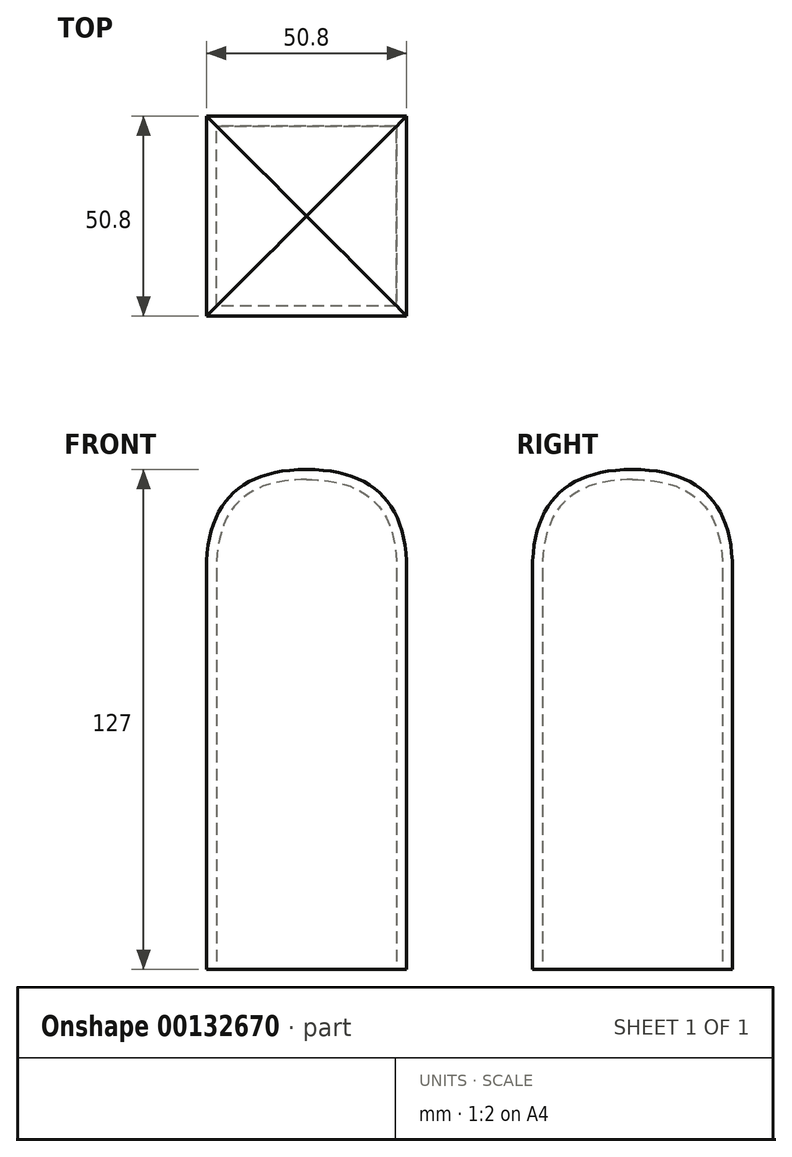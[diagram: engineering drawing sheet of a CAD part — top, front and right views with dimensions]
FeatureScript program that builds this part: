
annotation { "Feature Type Name" : "Feature", "Feature Type Description" : "" }
export const myFeature = defineFeature(function(context is Context, id is Id, definition is map)
    precondition{}
    {
        {
            var Q0;
            Q0=qCreatedBy(makeId("Top.planeOp"),FACE);
            var sketch = newSketch(context, id + "F0", { "sketchPlane" : qUnion([Q0])});
            skLineSegment(sketch, "E0.bottom", {"start": v(0, 0) * mm, "end": v(-50.8, 0) * mm});
            skLineSegment(sketch, "E0.top", {"start": v(0, 50.8) * mm, "end": v(-50.8, 50.8) * mm});
            skLineSegment(sketch, "E0.left", {"start": v(0, 0) * mm, "end": v(0, 50.8) * mm});
            skLineSegment(sketch, "E0.right", {"start": v(-50.8, 0) * mm, "end": v(-50.8, 50.8) * mm});
            skSolve(sketch);
        }
        {
            var Q0;
            Q0=makeQuery(id+"F0.imprint","IMPRINT",FACE,{"disambiguationData":[TD([[makeQuery(id+"F0.imprint","IMPRINT",EDGE,{"derivedFrom":sQuery(id+"F0.wireOp",EDGE,"E0.bottom")}),-1.0]])]});
            extrude(context, id + "F1", {"entities" : qUnion([Q0]), "depth" : 127 * mm});
        }
        {
            var Q0;
            Q0=makeQuery(id+"F1.opExtrude","CAP_EDGE",EDGE,{"disambiguationData":[OSD([sQuery(id+"F0.wireOp",EDGE,"E0.right")])],"isStart":false});
            var Q1;
            Q1=makeQuery(id+"F1.opExtrude","CAP_FACE",FACE,{"disambiguationData":[OSD([sQuery(id+"F0.wireOp",EDGE,"E0.bottom"),sQuery(id+"F0.wireOp",EDGE,"E0.top"),sQuery(id+"F0.wireOp",EDGE,"E0.left"),sQuery(id+"F0.wireOp",EDGE,"E0.right")])],"isStart":false});
            fillet(context, id + "F2", {"entities" : qUnion([Q0, Q1]), "radius" : 25.4 * mm, "tangentPropagation" : true, "rho" : 0.5, "crossSection" : FilletCrossSection.CONIC, "allowEdgeOverflow" : false});
        }
        {
            var Q0;
            Q0=makeQuery(id+"F1.opExtrude","CAP_FACE",FACE,{"disambiguationData":[OSD([sQuery(id+"F0.wireOp",EDGE,"E0.bottom"),sQuery(id+"F0.wireOp",EDGE,"E0.top"),sQuery(id+"F0.wireOp",EDGE,"E0.left"),sQuery(id+"F0.wireOp",EDGE,"E0.right")])],"isStart":true});
            shell(context, id + "F3", {"entities" : qUnion([Q0]), "thickness" : 2.54 * mm});
        }
    });
